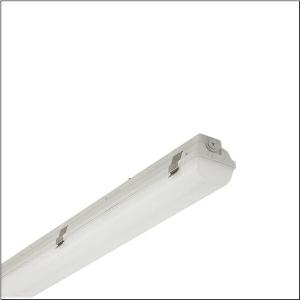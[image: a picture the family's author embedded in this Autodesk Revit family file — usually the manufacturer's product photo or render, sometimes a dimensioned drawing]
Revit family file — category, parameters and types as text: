
# Revit family: monsun_r__21_eco_51fj10dp47a_8000
name_source: partatom
category: Lighting Fixtures
units: mm (PartAtom-declared; Revit-internal decimal feet)

## family parameters
Cut with Voids When Loaded = No
Host = Face
Light Source = No
Part Type = Normal
Room Calculation Point = No
Round Connector Dimension = Use Diameter
Shared = No

## types (1)
- Monsun® 21 Eco (1 x LED, 7000 lm, 50 W, 4000K)
    Apparent Load = 50 VA
    CIE Flux Codes = 41 70 89 90 100
    Color Rendering = 80
    Color Temperature = 4000K
    Default Elevation = 1800 mm
    Description = Monsun® 21 Eco, damp-proof luminaire, primary optical cover: diffuser, of PMMA, frosted, light emission: direct distribution, primary light characteristic: symmetric, installation type: suspended mounting, surface-mounted, LED, rated luminous flux: 7.000lm, luminous efficacy: 140lm/W, light colour: 840, colour temperature: 4000K, control gear: ECG DALI, with terminal, 5-pole, max. 2.5mm², mains connection: 220..240V, AC, 50/60Hz, rated input power: 50W, housing, of glass-fibre reinforced polyester, light grey (RAL 7035), length: 1.577mm, width: 90mm, height: 95mm, clip for enclosure, of spring steel V2A, protection rating (complete): IP66, insulation class (complete): insulation class I (protective earthing), certification: CE, UKCA, protection symbol: D, impact resistance: IK02, permissible operating ambient temperature: -20..+35°C, corresponds to IFS (International Featured Standards) requirements for safety and quality in the food industry, contact your sales advisor before using the luminaires in applications with unclear chemical exposure, large temperature fluctuations or condensation-forming humidity, packaging unit: 1 piece
    Height = 103 mm
    Lamp = 1 x LED
    Lamp Light Flux = 7000 lm
    Lamp Power = 50 W
    Lamp count = 1
    Length = 1577 mm
    Luminous efficacy = 140 lm/W
    Manufacturer = Siteco
    ModVariant = No
    Model = 51FJ10DP47A
    Mounting Place = Ceiling
    Mounting Type = Surface mounted
    Number of Poles = 1
    OnlyDefault = Yes
    Power Factor = 1
    Product Name = Monsun® 21 Eco
    Product group = damp-proof luminaire
    ProductGroupID = 301
    Protection Class = Protection class I
    Protection Degree = IP 66
    RLX_Detail_Level = 1
    RLX_Emergency_Light_Flux = 0 lm
    RLX_Emergency_Type = 0
    RLX_Emergency_Type_DB = No
    RlxData = <blob elided: 33477 chars, md5=400cbc7d>
    Socket = socket
    Standby Power = 0 W
    System Light Flux = 7000 lm
    System Power = 50 W
    Type Comments = Product without accessories
    Type Image = l_1007218.jpg
    URL = http://relux.com
    VarID = ---
    Voltage = 0 V
    Weight = 0.00 kg
    Width = 90 mm

## geometry (parser evidence)
native form markers: Blend x4, Sweep x11
no freeform markers — native parametric forms only
